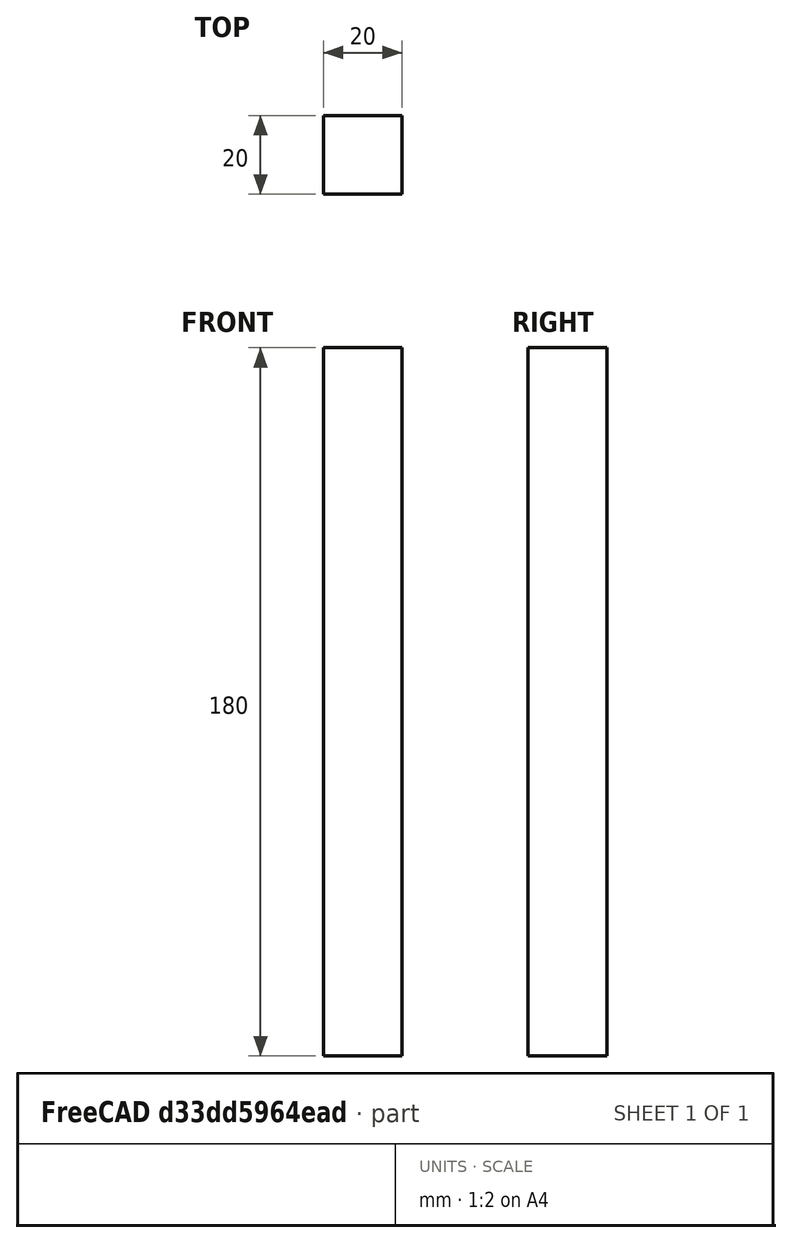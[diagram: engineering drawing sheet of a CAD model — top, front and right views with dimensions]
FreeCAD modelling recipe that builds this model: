
FCSTD DOCUMENT  (FreeCAD 0.19R24276 (Git))
Label: L180
License: All rights reserved
LicenseURL: http://en.wikipedia.org/wiki/All_rights_reserved
objects: Sketcher::SketchObject×1, PartDesign::Pad×1, PartDesign::Body×1
note: 4 computed .brp shape members not serialized (recipe doc carries the construction recipe); baked Part::Feature solids carry a one-line shape summary decoded from their .brp

FEATURE [Sketcher::SketchObject] Sketch
  FullyConstrained = true
  MapMode = 5
  Support = -> [XY_Plane]
  sketch-geometry (4):
    g0: LineSegment StartX=0 StartY=0 StartZ=0 EndX=20 EndY=0 EndZ=0
    g1: LineSegment StartX=20 StartY=0 StartZ=0 EndX=20 EndY=-20 EndZ=0
    g2: LineSegment StartX=20 StartY=-20 StartZ=0 EndX=0 EndY=-20 EndZ=0
    g3: LineSegment StartX=0 StartY=-20 StartZ=0 EndX=0 EndY=0 EndZ=0
  constraints (11):
    c: Coincident(g0,g1)
    c: Coincident(g1,g2)
    c: Coincident(g2,g3)
    c: Coincident(g3,g0)
    c: Horizontal(g0)
    c: Horizontal(g2)
    c: Vertical(g1)
    c: Vertical(g3)
    c: Coincident(g0,g-1)
    c: Equal(g2,g1)
    c: DistanceY(g1,g1) = 20
FEATURE [PartDesign::Pad] Pad
  Direction = (1,1,1)
  Length = 180
  Length2 = 100
  Profile = -> Sketch
  Type = 0
FEATURE [PartDesign::Body] Body
  Group = -> [Sketch,Pad]
  Origin = -> Origin
  Tip = -> Pad
